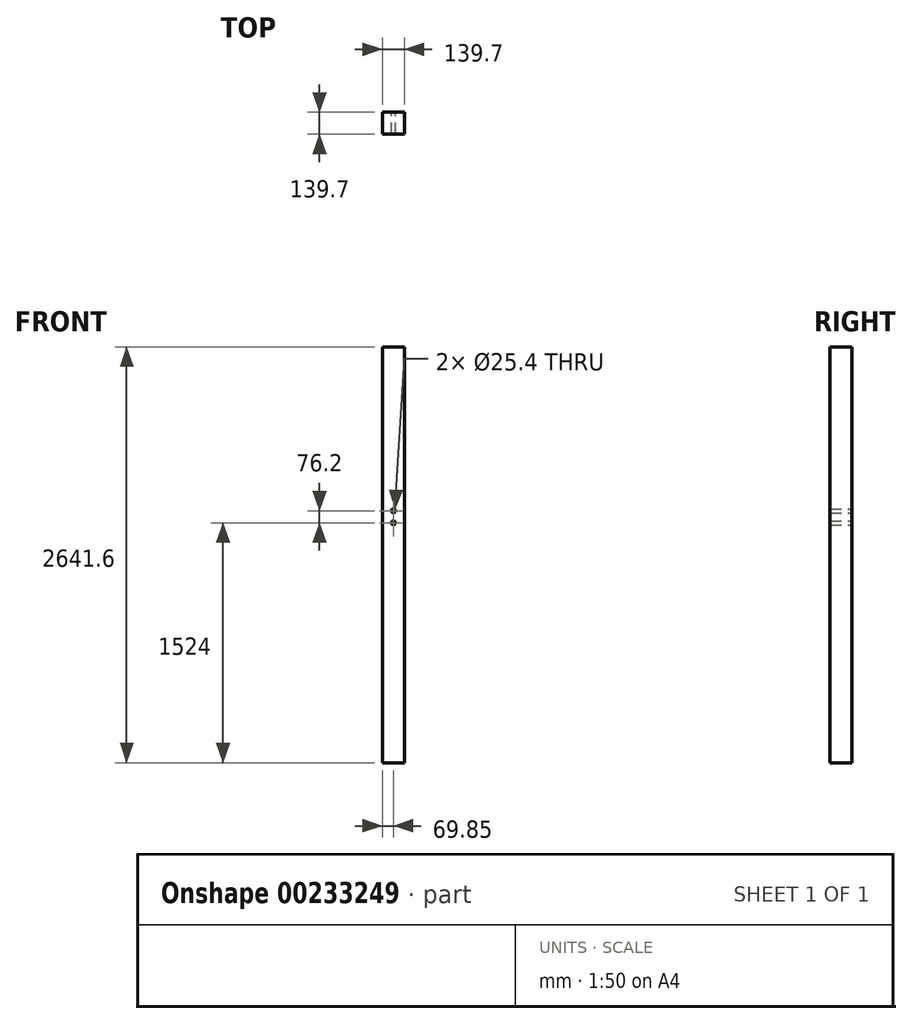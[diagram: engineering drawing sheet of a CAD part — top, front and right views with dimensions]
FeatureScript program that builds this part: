
annotation { "Feature Type Name" : "Feature", "Feature Type Description" : "" }
export const myFeature = defineFeature(function(context is Context, id is Id, definition is map)
    precondition{}
    {
        {
            var Q0;
            Q0=qCreatedBy(makeId("Front.planeOp"),FACE);
            var sketch = newSketch(context, id + "F0", { "sketchPlane" : qUnion([Q0])});
            skLineSegment(sketch, "E0.bottom", {"start": v(-69.85, 2462.3) * mm, "end": v(69.85, 2462.3) * mm});
            skLineSegment(sketch, "E0.top", {"start": v(-69.85, -179.3) * mm, "end": v(69.85, -179.3) * mm});
            skLineSegment(sketch, "E0.left", {"start": v(-69.85, 2462.3) * mm, "end": v(-69.85, -179.3) * mm});
            skLineSegment(sketch, "E0.right", {"start": v(69.85, 2462.3) * mm, "end": v(69.85, -179.3) * mm});
            skCircle(sketch, "E1", {"center": v(0, 1420.9) * mm, "radius": 12.7 * mm});
            skCircle(sketch, "E2", {"center": v(0, 1344.7) * mm, "radius": 12.7 * mm});
            skSolve(sketch);
        }
        {
            var Q0;
            Q0 = qSketchRegion(id + "F0", true);
            extrude(context, id + "F1", {"entities" : qUnion([Q0]), "depth" : 139.7 * mm});
        }
    });
